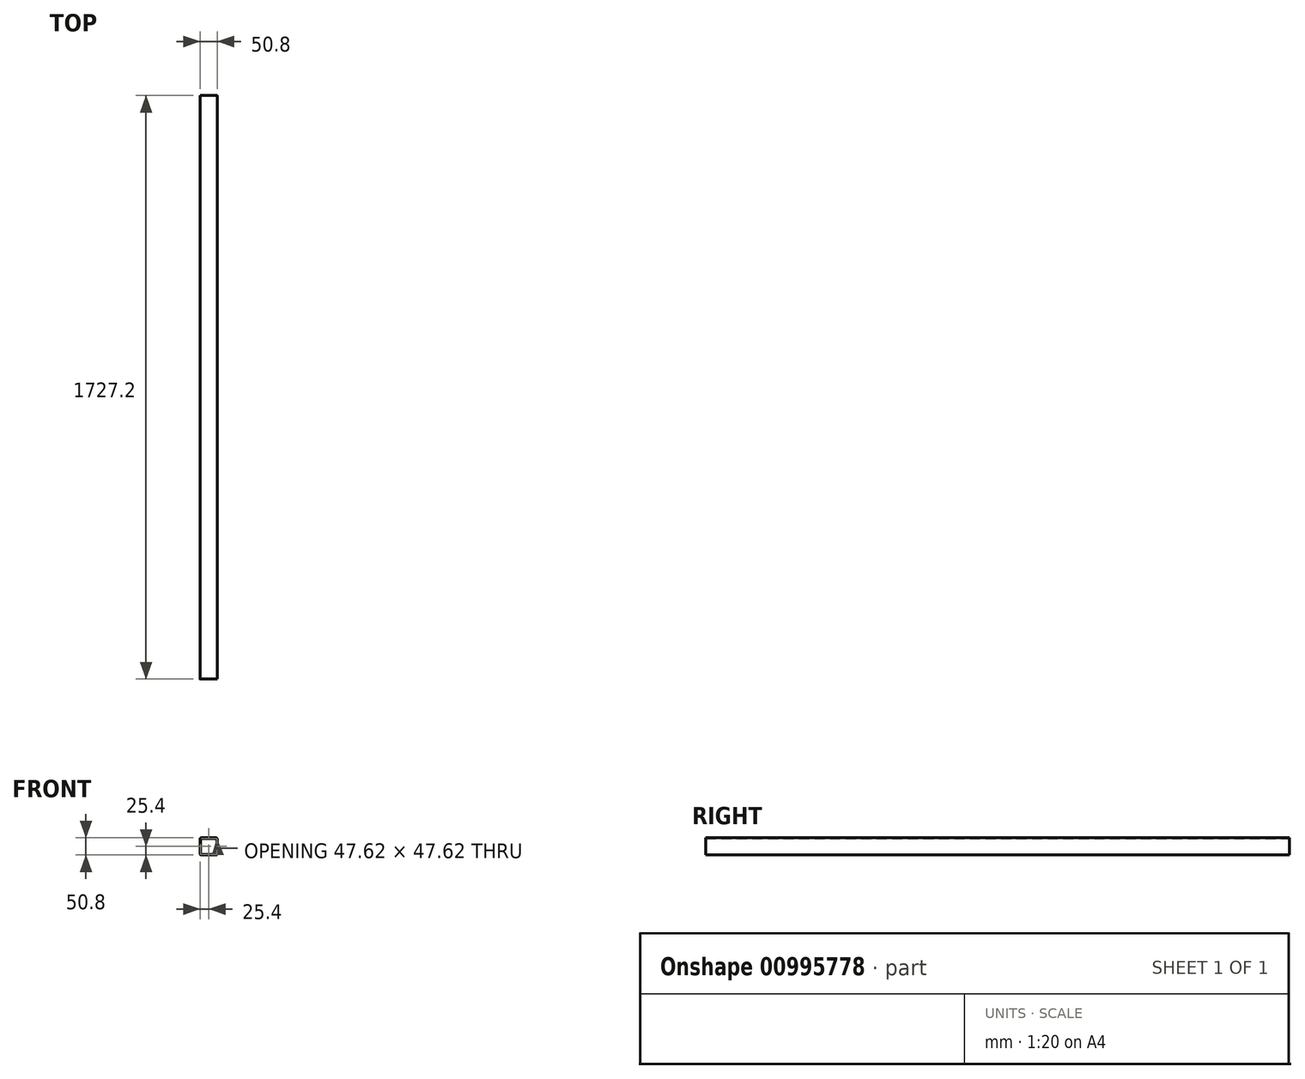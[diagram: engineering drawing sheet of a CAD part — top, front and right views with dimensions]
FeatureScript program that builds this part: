
annotation { "Feature Type Name" : "Feature", "Feature Type Description" : "" }
export const myFeature = defineFeature(function(context is Context, id is Id, definition is map)
    precondition{}
    {
        {
            var Q0;
            Q0=qCreatedBy(makeId("Front.planeOp"),FACE);
            var sketch = newSketch(context, id + "F0", { "sketchPlane" : qUnion([Q0])});
            skLineSegment(sketch, "E0.bottom", {"start": v(0, 0) * mm, "end": v(50.8, 0) * mm});
            skLineSegment(sketch, "E0.top", {"start": v(0, 50.8) * mm, "end": v(50.8, 50.8) * mm});
            skLineSegment(sketch, "E0.left", {"start": v(0, 0) * mm, "end": v(0, 50.8) * mm});
            skLineSegment(sketch, "E0.right", {"start": v(50.8, 0) * mm, "end": v(50.8, 50.8) * mm});
            skLineSegment(sketch, "E1.0", {"start": v(1.59, 1.59) * mm, "end": v(1.59, 49.21) * mm});
            skLineSegment(sketch, "E1.1", {"start": v(1.59, 1.59) * mm, "end": v(49.21, 1.59) * mm});
            skLineSegment(sketch, "E1.2", {"start": v(49.21, 1.59) * mm, "end": v(49.21, 49.21) * mm});
            skLineSegment(sketch, "E1.3", {"start": v(1.59, 49.21) * mm, "end": v(49.21, 49.21) * mm});
            skSolve(sketch);
        }
        {
            var Q0;
            Q0 = qSketchRegion(id + "F0", true);
            extrude(context, id + "F1", {"entities" : qUnion([Q0]), "depth" : 1727.2 * mm, "offsetDistance" : 25.4 * mm});
        }
        {
            var Q0;
            Q0=makeQuery(id+"F1.opExtrude","SWEPT_EDGE",EDGE,{"disambiguationData":[OSD([sQuery(id+"F0.wireOp",EDGE,"E0.top"),sQuery(id+"F0.wireOp",EDGE,"E0.left")])]});
            var Q1;
            Q1=makeQuery(id+"F1.opExtrude","SWEPT_EDGE",EDGE,{"disambiguationData":[OSD([sQuery(id+"F0.wireOp",EDGE,"E0.top"),sQuery(id+"F0.wireOp",EDGE,"E0.right")])]});
            var Q2;
            Q2=makeQuery(id+"F1.opExtrude","SWEPT_EDGE",EDGE,{"disambiguationData":[OSD([sQuery(id+"F0.wireOp",EDGE,"E0.bottom"),sQuery(id+"F0.wireOp",EDGE,"E0.right")])]});
            var Q3;
            Q3=makeQuery(id+"F1.opExtrude","SWEPT_EDGE",EDGE,{"disambiguationData":[OSD([sQuery(id+"F0.wireOp",EDGE,"E0.bottom"),sQuery(id+"F0.wireOp",EDGE,"E0.left")])]});
            fillet(context, id + "F2", {"entities" : qUnion([Q0, Q1, Q2, Q3]), "radius" : 3.17 * mm, "tangentPropagation" : true, "defaultsChanged" : true, "vertexSettings" : [], "allowEdgeOverflow" : false});
        }
        {
            var Q0;
            Q0=makeQuery(id+"F1.opExtrude","SWEPT_EDGE",EDGE,{"disambiguationData":[OSD([sQuery(id+"F0.wireOp",EDGE,"E1.0"),sQuery(id+"F0.wireOp",EDGE,"E1.3")])]});
            var Q1;
            Q1=makeQuery(id+"F1.opExtrude","SWEPT_EDGE",EDGE,{"disambiguationData":[OSD([sQuery(id+"F0.wireOp",EDGE,"E1.2"),sQuery(id+"F0.wireOp",EDGE,"E1.3")])]});
            var Q2;
            Q2=makeQuery(id+"F1.opExtrude","SWEPT_EDGE",EDGE,{"disambiguationData":[OSD([sQuery(id+"F0.wireOp",EDGE,"E1.0"),sQuery(id+"F0.wireOp",EDGE,"E1.1")])]});
            var Q3;
            Q3=makeQuery(id+"F1.opExtrude","SWEPT_EDGE",EDGE,{"disambiguationData":[OSD([sQuery(id+"F0.wireOp",EDGE,"E1.1"),sQuery(id+"F0.wireOp",EDGE,"E1.2")])]});
            fillet(context, id + "F3", {"entities" : qUnion([Q0, Q1, Q2, Q3]), "radius" : 1.59 * mm, "tangentPropagation" : true, "defaultsChanged" : true, "vertexSettings" : [], "allowEdgeOverflow" : false});
        }
    });
